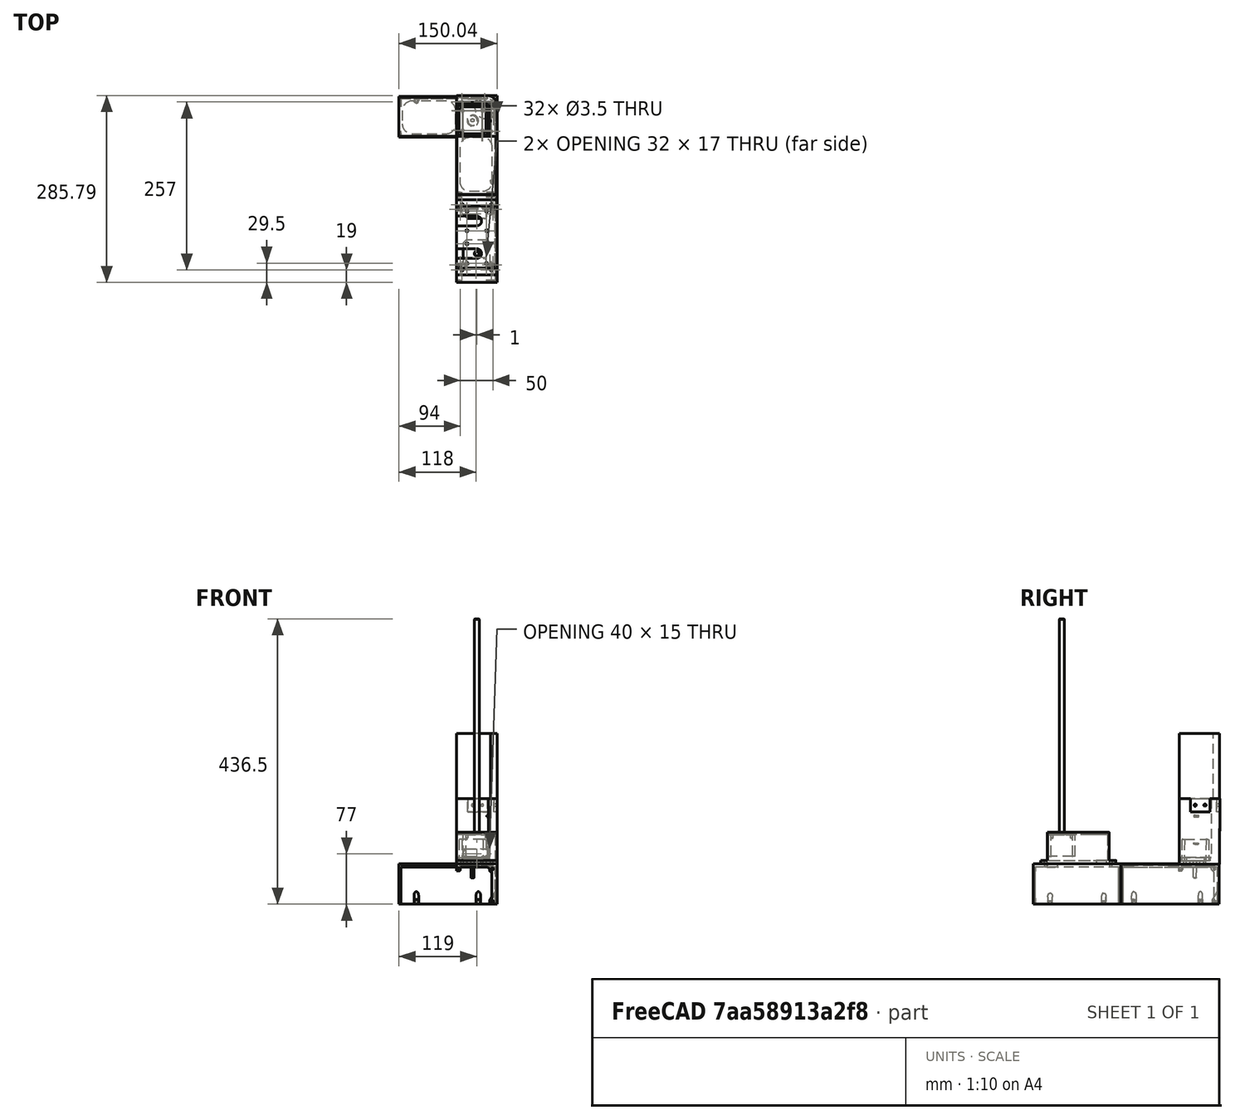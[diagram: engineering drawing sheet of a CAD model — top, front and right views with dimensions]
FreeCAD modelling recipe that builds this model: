
FCSTD DOCUMENT  (FreeCAD 0.21R33771 (Git))
Label: beggining_assembly
License: All rights reserved
LicenseURL: http://en.wikipedia.org/wiki/All_rights_reserved
objects: Part::FeaturePython×8, App::FeaturePython×8, Part::Feature×7
note: 14 computed .brp shape members not serialized (recipe doc carries the construction recipe); baked Part::Feature solids carry a one-line shape summary decoded from their .brp

FEATURE [Part::Feature] Solid  label="Pocket006"
  Placement = pos=(-7.50319,-6.96558,-61.0388) rot=(-0.964742,-0.000333,-0.263197;0.002624rad)
  shape: bbox 62.04 x 62.3 x 100.2 mm, 71 faces (baked)
FEATURE [Part::Feature] Solid001  label="Fillet001"
  Placement = pos=(-5.48766,36.1149,-23.1477) rot=(1,0,0;3.13906rad)
  shape: bbox 41 x 41.08 x 59.07 mm, 35 faces (baked)
FEATURE [Part::Feature] Part__Feature  label="Pocket002"
  Placement = pos=(-9.5,53,139) rot=(1,0,0;3.14159rad)
  shape: bbox 62 x 62 x 120 mm, 23 faces (baked)
FEATURE [Part::Feature] Part__Feature001  label="Fillet017"
  Placement = pos=(-97.5,52,-60.5) rot=(1,0,0;3.14159rad)
  shape: bbox 150 x 150 x 62 mm, 187 faces (baked)
FEATURE [Part::Feature] Part__Feature002  label="Fillet016"
  Placement = pos=(52.5,-232.5,-60.5) rot=(-0.707107,-0.707107,0;3.14159rad)
  shape: bbox 62 x 134 x 62 mm, 118 faces (baked)
FEATURE [Part::Feature] Part__Feature003  label="Fillet005"
  Placement = pos=(21.5,-163.5,-60.5) rot=(0,0,1;4.71239rad)
  shape: bbox 62 x 115 x 48 mm, 91 faces (baked)
FEATURE [Part::FeaturePython] Parts  # WARN: FeaturePython — macro-defined, semantics opaque (R4)
  Group = -> [Solid001,Solid,Part__Feature,Part__Feature001,Part__Feature002,Part__Feature003]
  GroupMode = 0
FEATURE [Part::Feature] Part__Feature004  label="Chamfer001"
  Placement = pos=(1,-209,-49) rot=(0,0,1;0rad)
  shape: bbox 41 x 41 x 363 mm, 29 faces (baked)
FEATURE [Part::FeaturePython] Assembly  # WARN: FeaturePython — macro-defined, semantics opaque (R4)
  AutoRelax = true
  BuildShape = 0
  Freeze = false
  Group = -> [Constraints,Elements,Parts]
  Verbose = false
  _SolverType = 1
  _Version = 1
FEATURE [App::FeaturePython] Constraints  # WARN: FeaturePython — macro-defined, semantics opaque (R4)
  Group = -> [Constraint,Constraint001]
  _Version = 1
FEATURE [App::FeaturePython] Elements  # WARN: FeaturePython — macro-defined, semantics opaque (R4)
  Group = -> [_Element,_Element001,_Element002,_Element003,_Element004,_Element005]
FEATURE [App::FeaturePython] Constraint  label="PlaneCoincident"  # WARN: FeaturePython — macro-defined, semantics opaque (R4)
  Angle = 0
  AnglePitch = 0
  AngleRoll = 0
  Cascade = false
  Disabled = false
  Group = -> [ElementLink,ElementLink001]
  LockAngle = false
  Multiply = false
  OffsetX = 0
  OffsetY = 0
  _ConstraintType = 35
  _Parent = -> Constraints
FEATURE [App::FeaturePython] ElementLink  label="_Element"  # link proxy (typed FeaturePython)
  LinkTransform = true
  LinkedObject = -> _Element
  _Parent = -> Constraint
FEATURE [Part::FeaturePython] _Element  # link proxy (typed FeaturePython)
  Detach = false
  LinkTransform = true
  LinkedObject = -> Solid001 [Face3]
  _Parent = -> Elements
FEATURE [App::FeaturePython] ElementLink001  label="_Element001"  # link proxy (typed FeaturePython)
  LinkTransform = true
  LinkedObject = -> _Element001
  _Parent = -> Constraint
FEATURE [Part::FeaturePython] _Element001  # link proxy (typed FeaturePython)
  Detach = false
  LinkTransform = true
  LinkedObject = -> Solid [Face32]
  _Parent = -> Elements
FEATURE [App::FeaturePython] Constraint001  label="PlaneAlignment"  # WARN: FeaturePython — macro-defined, semantics opaque (R4)
  Angle = 0
  AnglePitch = 0
  AngleRoll = 0
  Cascade = false
  Disabled = false
  Group = -> [ElementLink002,ElementLink003]
  LockAngle = false
  _ConstraintType = 37
  _Parent = -> Constraints
FEATURE [App::FeaturePython] ElementLink002  label="_Element002"  # link proxy (typed FeaturePython)
  LinkTransform = true
  LinkedObject = -> _Element002
  _Parent = -> Constraint001
FEATURE [Part::FeaturePython] _Element002  # link proxy (typed FeaturePython)
  Detach = false
  LinkTransform = true
  LinkedObject = -> Solid [Face49]
  _Parent = -> Elements
FEATURE [App::FeaturePython] ElementLink003  label="_Element003"  # link proxy (typed FeaturePython)
  LinkTransform = true
  LinkedObject = -> _Element003
  _Parent = -> Constraint001
FEATURE [Part::FeaturePython] _Element003  # link proxy (typed FeaturePython)
  Detach = false
  LinkTransform = true
  LinkedObject = -> Solid001 [Face16]
  _Parent = -> Elements
FEATURE [Part::FeaturePython] _Element004  # link proxy (typed FeaturePython)
  Detach = false
  LinkTransform = true
  LinkedObject = -> Solid [Face25]
  _Parent = -> Elements
FEATURE [Part::FeaturePython] _Element005  # link proxy (typed FeaturePython)
  Detach = false
  LinkTransform = true
  LinkedObject = -> Part__Feature [Face12]
  _Parent = -> Elements
